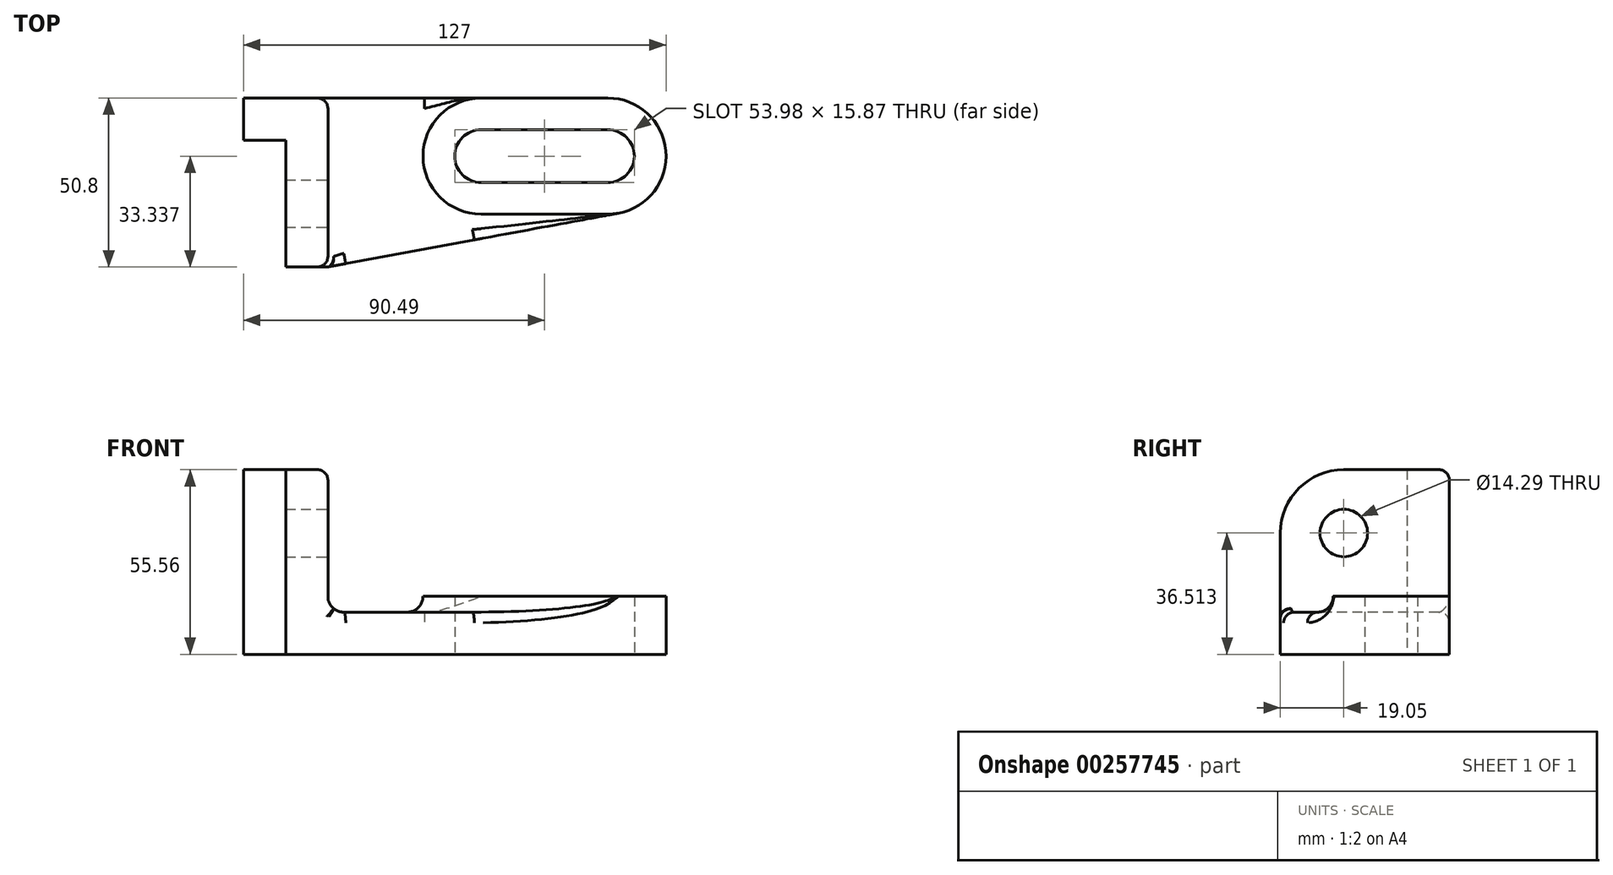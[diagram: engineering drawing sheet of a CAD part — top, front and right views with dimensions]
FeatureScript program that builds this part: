
annotation { "Feature Type Name" : "Feature", "Feature Type Description" : "" }
export const myFeature = defineFeature(function(context is Context, id is Id, definition is map)
    precondition{}
    {
        {
            var Q0;
            Q0=qCreatedBy(makeId("Top.planeOp"),FACE);
            var sketch = newSketch(context, id + "F0", { "sketchPlane" : qUnion([Q0])});
            skLineSegment(sketch, "E0", {"start": v(-57.56, -50.8) * mm, "end": v(-44.86, -50.8) * mm});
            skArc(sketch, "E1", {"start": v(1.18, -9.52) * mm, "mid": v(-6.76, -17.46) * mm, "end": v(1.18, -25.4) * mm});
            skArc(sketch, "E2", {"start": v(39.28, -25.4) * mm, "mid": v(47.22, -17.46) * mm, "end": v(39.28, -9.52) * mm});
            skArc(sketch, "E3", {"start": v(1.18, 0) * mm, "mid": v(-16.28, -17.46) * mm, "end": v(1.18, -34.92) * mm});
            skArc(sketch, "E4", {"start": v(39.28, -34.92) * mm, "mid": v(56.74, -17.46) * mm, "end": v(39.28, 0) * mm});
            skLineSegment(sketch, "E5", {"start": v(1.18, -9.52) * mm, "end": v(39.28, -9.52) * mm});
            skLineSegment(sketch, "E6", {"start": v(1.18, -25.4) * mm, "end": v(39.28, -25.4) * mm});
            skLineSegment(sketch, "E7", {"start": v(1.18, 0) * mm, "end": v(39.28, 0) * mm});
            skLineSegment(sketch, "E8", {"start": v(1.18, -34.92) * mm, "end": v(39.28, -34.92) * mm});
            skLineSegment(sketch, "E9", {"start": v(-44.86, -50.8) * mm, "end": v(-44.86, 0) * mm});
            skLineSegment(sketch, "E10", {"start": v(-44.86, 0) * mm, "end": v(-70.26, 0) * mm});
            skLineSegment(sketch, "E11", {"start": v(-70.26, 0) * mm, "end": v(-70.26, -12.7) * mm});
            skLineSegment(sketch, "E12", {"start": v(-70.26, -12.7) * mm, "end": v(-57.56, -12.7) * mm});
            skLineSegment(sketch, "E13", {"start": v(-57.56, -12.7) * mm, "end": v(-57.56, -50.8) * mm});
            skLineSegment(sketch, "E14", {"start": v(-44.86, -50.8) * mm, "end": v(42.46, -34.63) * mm});
            skLineSegment(sketch, "E15", {"start": v(-44.86, 0) * mm, "end": v(1.18, 0) * mm});
            skSolve(sketch);
        }
        {
            var Q0;
            Q0 = qSketchRegion(id + "F0", true);
            extrude(context, id + "F1", {"entities" : qUnion([Q0]), "depth" : 12.7 * mm});
        }
        {
            var Q0;
            Q0=makeQuery(id+"F0.imprint","IMPRINT",FACE,{"disambiguationData":[TD([[makeQuery(id+"F0.imprint","IMPRINT",EDGE,{"derivedFrom":sQuery(id+"F0.wireOp",EDGE,"E1")}),-1.0]])]});
            extrude(context, id + "F2", {"entities" : qUnion([Q0]), "operationType" : NewBodyOperationType.ADD, "depth" : 17.46 * mm});
        }
        {
            var Q0;
            Q0=makeQuery(id+"F2.boolean.opBoolean","INTERSECT",EDGE,{"derivedFrom":[makeQuery(id+"F1.opExtrude","CAP_FACE",FACE,{"disambiguationData":[OSD([sQuery(id+"F0.wireOp",EDGE,"E0"),sQuery(id+"F0.wireOp",EDGE,"E1"),sQuery(id+"F0.wireOp",EDGE,"E2"),sQuery(id+"F0.wireOp",EDGE,"E4"),sQuery(id+"F0.wireOp",EDGE,"E5"),sQuery(id+"F0.wireOp",EDGE,"E6"),sQuery(id+"F0.wireOp",EDGE,"E7"),sQuery(id+"F0.wireOp",EDGE,"E10"),sQuery(id+"F0.wireOp",EDGE,"E11"),sQuery(id+"F0.wireOp",EDGE,"E12"),sQuery(id+"F0.wireOp",EDGE,"E13"),sQuery(id+"F0.wireOp",EDGE,"E14"),sQuery(id+"F0.wireOp",EDGE,"E15")])],"isStart":false}),makeQuery(id+"F2.opExtrude","SWEPT_FACE",FACE,{"disambiguationData":[OSD([sQuery(id+"F0.wireOp",EDGE,"E8")])]})]});
            var Q1;
            Q1=makeQuery(id+"F2.boolean.opBoolean","INTERSECT",EDGE,{"derivedFrom":[makeQuery(id+"F1.opExtrude","CAP_FACE",FACE,{"disambiguationData":[OSD([sQuery(id+"F0.wireOp",EDGE,"E0"),sQuery(id+"F0.wireOp",EDGE,"E1"),sQuery(id+"F0.wireOp",EDGE,"E2"),sQuery(id+"F0.wireOp",EDGE,"E4"),sQuery(id+"F0.wireOp",EDGE,"E5"),sQuery(id+"F0.wireOp",EDGE,"E6"),sQuery(id+"F0.wireOp",EDGE,"E7"),sQuery(id+"F0.wireOp",EDGE,"E10"),sQuery(id+"F0.wireOp",EDGE,"E11"),sQuery(id+"F0.wireOp",EDGE,"E12"),sQuery(id+"F0.wireOp",EDGE,"E13"),sQuery(id+"F0.wireOp",EDGE,"E14"),sQuery(id+"F0.wireOp",EDGE,"E15")])],"isStart":false}),makeQuery(id+"F2.opExtrude","SWEPT_FACE",FACE,{"disambiguationData":[OSD([sQuery(id+"F0.wireOp",EDGE,"E3")])]})]});
            fillet(context, id + "F3", {"entities" : qUnion([Q0, Q1]), "radius" : 4.76 * mm, "tangentPropagation" : true, "allowEdgeOverflow" : false});
        }
        {
            var Q0;
            Q0=makeQuery(id+"F0.imprint","IMPRINT",FACE,{"disambiguationData":[TD([[makeQuery(id+"F0.imprint","IMPRINT",EDGE,{"derivedFrom":sQuery(id+"F0.wireOp",EDGE,"E0")}),1.0]])]});
            extrude(context, id + "F4", {"entities" : qUnion([Q0]), "operationType" : NewBodyOperationType.ADD, "depth" : 55.56 * mm});
        }
        {
            var Q0;
            Q0=makeQuery(id+"F4.boolean.opBoolean","INTERSECT",EDGE,{"derivedFrom":[makeQuery(id+"F1.opExtrude","CAP_FACE",FACE,{"disambiguationData":[OSD([sQuery(id+"F0.wireOp",EDGE,"E0"),sQuery(id+"F0.wireOp",EDGE,"E1"),sQuery(id+"F0.wireOp",EDGE,"E2"),sQuery(id+"F0.wireOp",EDGE,"E4"),sQuery(id+"F0.wireOp",EDGE,"E5"),sQuery(id+"F0.wireOp",EDGE,"E6"),sQuery(id+"F0.wireOp",EDGE,"E7"),sQuery(id+"F0.wireOp",EDGE,"E10"),sQuery(id+"F0.wireOp",EDGE,"E11"),sQuery(id+"F0.wireOp",EDGE,"E12"),sQuery(id+"F0.wireOp",EDGE,"E13"),sQuery(id+"F0.wireOp",EDGE,"E14"),sQuery(id+"F0.wireOp",EDGE,"E15")])],"isStart":false}),makeQuery(id+"F4.opExtrude","SWEPT_FACE",FACE,{"disambiguationData":[OSD([sQuery(id+"F0.wireOp",EDGE,"E9")])]})]});
            fillet(context, id + "F5", {"entities" : qUnion([Q0]), "radius" : 4.76 * mm, "tangentPropagation" : true, "allowEdgeOverflow" : false});
        }
        {
            var Q0;
            Q0=makeQuery(id+"F4.opExtrude","SWEPT_FACE",FACE,{"disambiguationData":[OSD([sQuery(id+"F0.wireOp",EDGE,"E9")])]});
            var sketch = newSketch(context, id + "F6", { "sketchPlane" : qUnion([Q0])});
            skCircle(sketch, "E16", {"center": v(-31.75, 36.51) * mm, "radius": 7.14 * mm});
            skSolve(sketch);
        }
        {
            var Q0;
            Q0=makeQuery(id+"F1.opExtrude","CAP_EDGE",EDGE,{"disambiguationData":[OSD([sQuery(id+"F0.wireOp",EDGE,"E14")])],"isStart":false});
            var Q1;
            {var subQ0=sQuery(id+"F0.wireOp",EDGE,"E14");Q1=makeQuery(id+"F3.opFillet","BLEND_EDGE",EDGE,{"blendedFrom":[makeQuery(id+"F2.boolean.opBoolean","INTERSECT",EDGE,{"derivedFrom":[makeQuery(id+"F1.opExtrude","CAP_FACE",FACE,{"disambiguationData":[OSD([sQuery(id+"F0.wireOp",EDGE,"E0"),sQuery(id+"F0.wireOp",EDGE,"E1"),sQuery(id+"F0.wireOp",EDGE,"E2"),sQuery(id+"F0.wireOp",EDGE,"E4"),sQuery(id+"F0.wireOp",EDGE,"E5"),sQuery(id+"F0.wireOp",EDGE,"E6"),sQuery(id+"F0.wireOp",EDGE,"E7"),sQuery(id+"F0.wireOp",EDGE,"E10"),sQuery(id+"F0.wireOp",EDGE,"E11"),sQuery(id+"F0.wireOp",EDGE,"E12"),sQuery(id+"F0.wireOp",EDGE,"E13"),subQ0,sQuery(id+"F0.wireOp",EDGE,"E15")])],"isStart":false}),makeQuery(id+"F2.opExtrude","SWEPT_FACE",FACE,{"disambiguationData":[OSD([sQuery(id+"F0.wireOp",EDGE,"E8")])]})]}),makeQuery(id+"F1.opExtrude","SWEPT_FACE",FACE,{"disambiguationData":[OSD([subQ0])]})],"blendedInto":[makeQuery(id+"F1.opExtrude","SWEPT_FACE",FACE,{"disambiguationData":[OSD([subQ0])]})]});}
            var Q2;
            {var subQ0=sQuery(id+"F0.wireOp",EDGE,"E14");var subQ1=sQuery(id+"F0.wireOp",EDGE,"E4");Q2=makeQuery(id+"F3.opFillet","BLEND_EDGE",EDGE,{"blendedFrom":[makeQuery(id+"F2.boolean.opBoolean","INTERSECT",EDGE,{"derivedFrom":[makeQuery(id+"F1.opExtrude","CAP_FACE",FACE,{"disambiguationData":[OSD([sQuery(id+"F0.wireOp",EDGE,"E0"),sQuery(id+"F0.wireOp",EDGE,"E1"),sQuery(id+"F0.wireOp",EDGE,"E2"),subQ1,sQuery(id+"F0.wireOp",EDGE,"E5"),sQuery(id+"F0.wireOp",EDGE,"E6"),sQuery(id+"F0.wireOp",EDGE,"E7"),sQuery(id+"F0.wireOp",EDGE,"E10"),sQuery(id+"F0.wireOp",EDGE,"E11"),sQuery(id+"F0.wireOp",EDGE,"E12"),sQuery(id+"F0.wireOp",EDGE,"E13"),subQ0,sQuery(id+"F0.wireOp",EDGE,"E15")])],"isStart":false}),makeQuery(id+"F2.opExtrude","SWEPT_FACE",FACE,{"disambiguationData":[OSD([subQ1])]})]}),makeQuery(id+"F1.opExtrude","SWEPT_FACE",FACE,{"disambiguationData":[OSD([subQ0])]})],"blendedInto":[makeQuery(id+"F1.opExtrude","SWEPT_FACE",FACE,{"disambiguationData":[OSD([subQ0])]})]});}
            var Q3;
            Q3=makeQuery(id+"F1.opExtrude","CAP_EDGE",EDGE,{"disambiguationData":[OSD([sQuery(id+"F0.wireOp",EDGE,"E7"),sQuery(id+"F0.wireOp",EDGE,"E10"),sQuery(id+"F0.wireOp",EDGE,"E15")])],"isStart":false});
            var Q4;
            {var subQ0=sQuery(id+"F0.wireOp",EDGE,"E7");var subQ1=sQuery(id+"F0.wireOp",EDGE,"E15");var subQ2=sQuery(id+"F0.wireOp",EDGE,"E10");Q4=makeQuery(id+"F3.opFillet","BLEND_EDGE",EDGE,{"blendedFrom":[makeQuery(id+"F2.boolean.opBoolean","INTERSECT",EDGE,{"derivedFrom":[makeQuery(id+"F1.opExtrude","CAP_FACE",FACE,{"disambiguationData":[OSD([sQuery(id+"F0.wireOp",EDGE,"E0"),sQuery(id+"F0.wireOp",EDGE,"E1"),sQuery(id+"F0.wireOp",EDGE,"E2"),sQuery(id+"F0.wireOp",EDGE,"E4"),sQuery(id+"F0.wireOp",EDGE,"E5"),sQuery(id+"F0.wireOp",EDGE,"E6"),subQ0,subQ2,sQuery(id+"F0.wireOp",EDGE,"E11"),sQuery(id+"F0.wireOp",EDGE,"E12"),sQuery(id+"F0.wireOp",EDGE,"E13"),sQuery(id+"F0.wireOp",EDGE,"E14"),subQ1])],"isStart":false}),makeQuery(id+"F2.opExtrude","SWEPT_FACE",FACE,{"disambiguationData":[OSD([sQuery(id+"F0.wireOp",EDGE,"E3")])]})]}),makeQuery(id+"F2.boolean.opBoolean","MERGE",FACE,{"derivedFrom":[makeQuery(id+"F1.opExtrude","SWEPT_FACE",FACE,{"disambiguationData":[OSD([subQ0,subQ2,subQ1])]}),makeQuery(id+"F2.opExtrude","SWEPT_FACE",FACE,{"disambiguationData":[OSD([subQ0])]})]})],"blendedInto":[makeQuery(id+"F2.boolean.opBoolean","MERGE",FACE,{"derivedFrom":[makeQuery(id+"F1.opExtrude","SWEPT_FACE",FACE,{"disambiguationData":[OSD([subQ0,subQ2,subQ1])]}),makeQuery(id+"F2.opExtrude","SWEPT_FACE",FACE,{"disambiguationData":[OSD([subQ0])]})]})]});}
            var Q5;
            Q5=makeQuery(id+"F4.opExtrude","SWEPT_EDGE",EDGE,{"disambiguationData":[OSD([sQuery(id+"F0.wireOp",EDGE,"E9"),sQuery(id+"F0.wireOp",EDGE,"E10"),sQuery(id+"F0.wireOp",EDGE,"E15")])]});
            var Q6;
            Q6=makeQuery(id+"F4.opExtrude","CAP_EDGE",EDGE,{"disambiguationData":[OSD([sQuery(id+"F0.wireOp",EDGE,"E10")])],"isStart":false});
            var Q7;
            {var subQ0=sQuery(id+"F0.wireOp",EDGE,"E10");var subQ1=sQuery(id+"F0.wireOp",EDGE,"E7");var subQ2=sQuery(id+"F0.wireOp",EDGE,"E15");Q7=makeQuery(id+"F5.opFillet","BLEND_EDGE",EDGE,{"blendedFrom":[makeQuery(id+"F4.boolean.opBoolean","INTERSECT",EDGE,{"derivedFrom":[makeQuery(id+"F1.opExtrude","CAP_FACE",FACE,{"disambiguationData":[OSD([sQuery(id+"F0.wireOp",EDGE,"E0"),sQuery(id+"F0.wireOp",EDGE,"E1"),sQuery(id+"F0.wireOp",EDGE,"E2"),sQuery(id+"F0.wireOp",EDGE,"E4"),sQuery(id+"F0.wireOp",EDGE,"E5"),sQuery(id+"F0.wireOp",EDGE,"E6"),subQ1,subQ0,sQuery(id+"F0.wireOp",EDGE,"E11"),sQuery(id+"F0.wireOp",EDGE,"E12"),sQuery(id+"F0.wireOp",EDGE,"E13"),sQuery(id+"F0.wireOp",EDGE,"E14"),subQ2])],"isStart":false}),makeQuery(id+"F4.opExtrude","SWEPT_FACE",FACE,{"disambiguationData":[OSD([sQuery(id+"F0.wireOp",EDGE,"E9")])]})]}),makeQuery(id+"F4.boolean.opBoolean","MERGE",FACE,{"derivedFrom":[makeQuery(id+"F2.boolean.opBoolean","MERGE",FACE,{"derivedFrom":[makeQuery(id+"F1.opExtrude","SWEPT_FACE",FACE,{"disambiguationData":[OSD([subQ1,subQ0,subQ2])]}),makeQuery(id+"F2.opExtrude","SWEPT_FACE",FACE,{"disambiguationData":[OSD([subQ1])]})]}),makeQuery(id+"F4.opExtrude","SWEPT_FACE",FACE,{"disambiguationData":[OSD([subQ0])]})]})],"blendedInto":[makeQuery(id+"F4.boolean.opBoolean","MERGE",FACE,{"derivedFrom":[makeQuery(id+"F2.boolean.opBoolean","MERGE",FACE,{"derivedFrom":[makeQuery(id+"F1.opExtrude","SWEPT_FACE",FACE,{"disambiguationData":[OSD([subQ1,subQ0,subQ2])]}),makeQuery(id+"F2.opExtrude","SWEPT_FACE",FACE,{"disambiguationData":[OSD([subQ1])]})]}),makeQuery(id+"F4.opExtrude","SWEPT_FACE",FACE,{"disambiguationData":[OSD([subQ0])]})]})]});}
            var Q8;
            Q8=makeQuery(id+"F4.opExtrude","CAP_EDGE",EDGE,{"disambiguationData":[OSD([sQuery(id+"F0.wireOp",EDGE,"E9")])],"isStart":false});
            var Q9;
            Q9=makeQuery(id+"F4.opExtrude","SWEPT_EDGE",EDGE,{"disambiguationData":[OSD([sQuery(id+"F0.wireOp",EDGE,"E0"),sQuery(id+"F0.wireOp",EDGE,"E9"),sQuery(id+"F0.wireOp",EDGE,"E14")])]});
            fillet(context, id + "F7", {"entities" : qUnion([Q0, Q1, Q2, Q3, Q4, Q5, Q6, Q7, Q8, Q9]), "radius" : 3.17 * mm, "tangentPropagation" : true, "allowEdgeOverflow" : false});
        }
        {
            var Q0;
            Q0=makeQuery(id+"F4.opExtrude","CAP_EDGE",EDGE,{"disambiguationData":[OSD([sQuery(id+"F0.wireOp",EDGE,"E0")])],"isStart":false});
            fillet(context, id + "F8", {"entities" : qUnion([Q0]), "radius" : 19.05 * mm, "tangentPropagation" : true, "allowEdgeOverflow" : false});
        }
        {
            var Q0;
            Q0=makeQuery(id+"F1.opExtrude","SWEPT_EDGE",EDGE,{"disambiguationData":[OSD([sQuery(id+"F0.wireOp",EDGE,"E0"),sQuery(id+"F0.wireOp",EDGE,"E9"),sQuery(id+"F0.wireOp",EDGE,"E14")])]});
            fillet(context, id + "F9", {"entities" : qUnion([Q0]), "radius" : 3.17 * mm, "tangentPropagation" : true, "allowEdgeOverflow" : false});
        }
        {
            var Q0;
            Q0=makeQuery(id+"F6.imprint","IMPRINT",FACE,{"disambiguationData":[TD([[makeQuery(id+"F6.imprint","IMPRINT",EDGE,{"derivedFrom":sQuery(id+"F6.wireOp",EDGE,"E16")}),1.0]])]});
            extrude(context, id + "F10", {"entities" : qUnion([Q0]), "operationType" : NewBodyOperationType.REMOVE, "oppositeDirection" : true, "depth" : 25.4 * mm});
        }
    });
